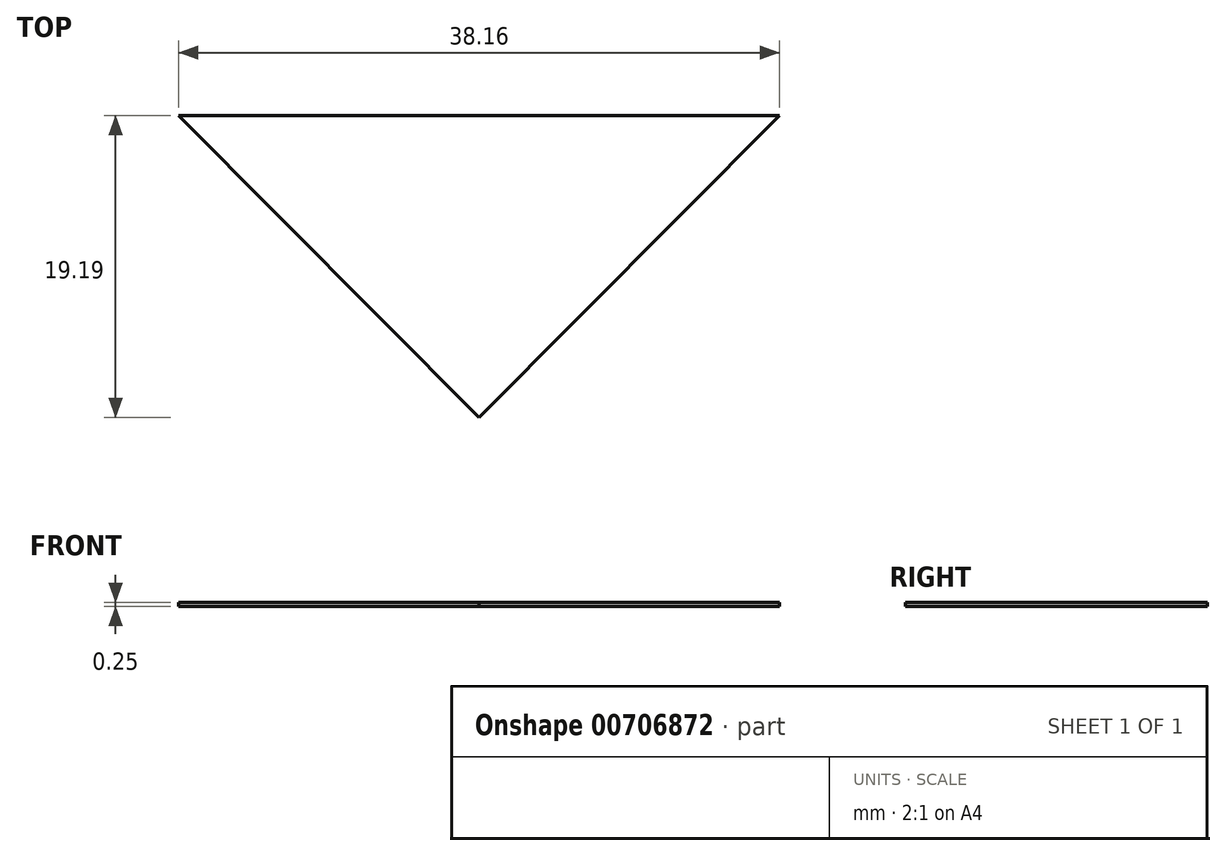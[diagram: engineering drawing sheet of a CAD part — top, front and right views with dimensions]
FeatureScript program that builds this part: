
annotation { "Feature Type Name" : "Feature", "Feature Type Description" : "" }
export const myFeature = defineFeature(function(context is Context, id is Id, definition is map)
    precondition{}
    {
        {
            var Q0;
            Q0=qCreatedBy(makeId("Top.planeOp"),FACE);
            var sketch = newSketch(context, id + "F0", { "sketchPlane" : qUnion([Q0])});
            skLineSegment(sketch, "E0", {"start": v(-63.51, 10.4) * mm, "end": v(-44.43, 29.6) * mm});
            skLineSegment(sketch, "E1", {"start": v(-63.51, 10.4) * mm, "end": v(-82.6, 29.6) * mm});
            skLineSegment(sketch, "E2", {"start": v(-82.6, 29.6) * mm, "end": v(-44.43, 29.6) * mm});
            skSolve(sketch);
        }
        {
            var Q0;
            Q0 = qSketchRegion(id + "F0", true);
            extrude(context, id + "F1", {"entities" : qUnion([Q0]), "depth" : 0.25 * mm, "offsetDistance" : 25.4 * mm});
        }
    });
